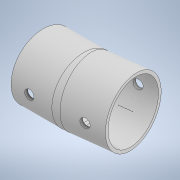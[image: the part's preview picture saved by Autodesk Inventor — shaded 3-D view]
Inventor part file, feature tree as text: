
AUTODESK INVENTOR PART (.ipt)
format: ipt  version: 2022 (Build 260153000, 153)  size: 245,248 bytes
history: native  units: mm
features: sketch x4, extrude x2, sweep x1
ambient origin geometry x8: Origin, YZ Plane, XZ Plane, XY Plane, X Axis, Y Axis, Z Axis, Center Point
bodies: Body1 (feature_tree)
feature tree (7):
  sweep  "Sweep1"
  extrude  "Extrusion8"  Depth=30.194196mm
  extrude  "Extrusion9"  Depth=10.0mm
  sketch  "Sketch5"  dims[d31=34.456mm d122=14.0mm]
  sketch  "Sketch6"  dims[d123=14.0mm d124=30.194196mm]
  sketch  "Sketch7"  dims[d125=10.0mm d126=19.0mm]
  sketch  "Sketch8"  dims[d127=21.0mm d128=0.0mm d129=0.0mm d130=6.0mm d131=3.0mm d132=25.0mm d133=0.0mm d134=6.0mm d135=3.0mm d136=25.0mm d137=0.0mm d138=0.01mm d139=0.01mm]
